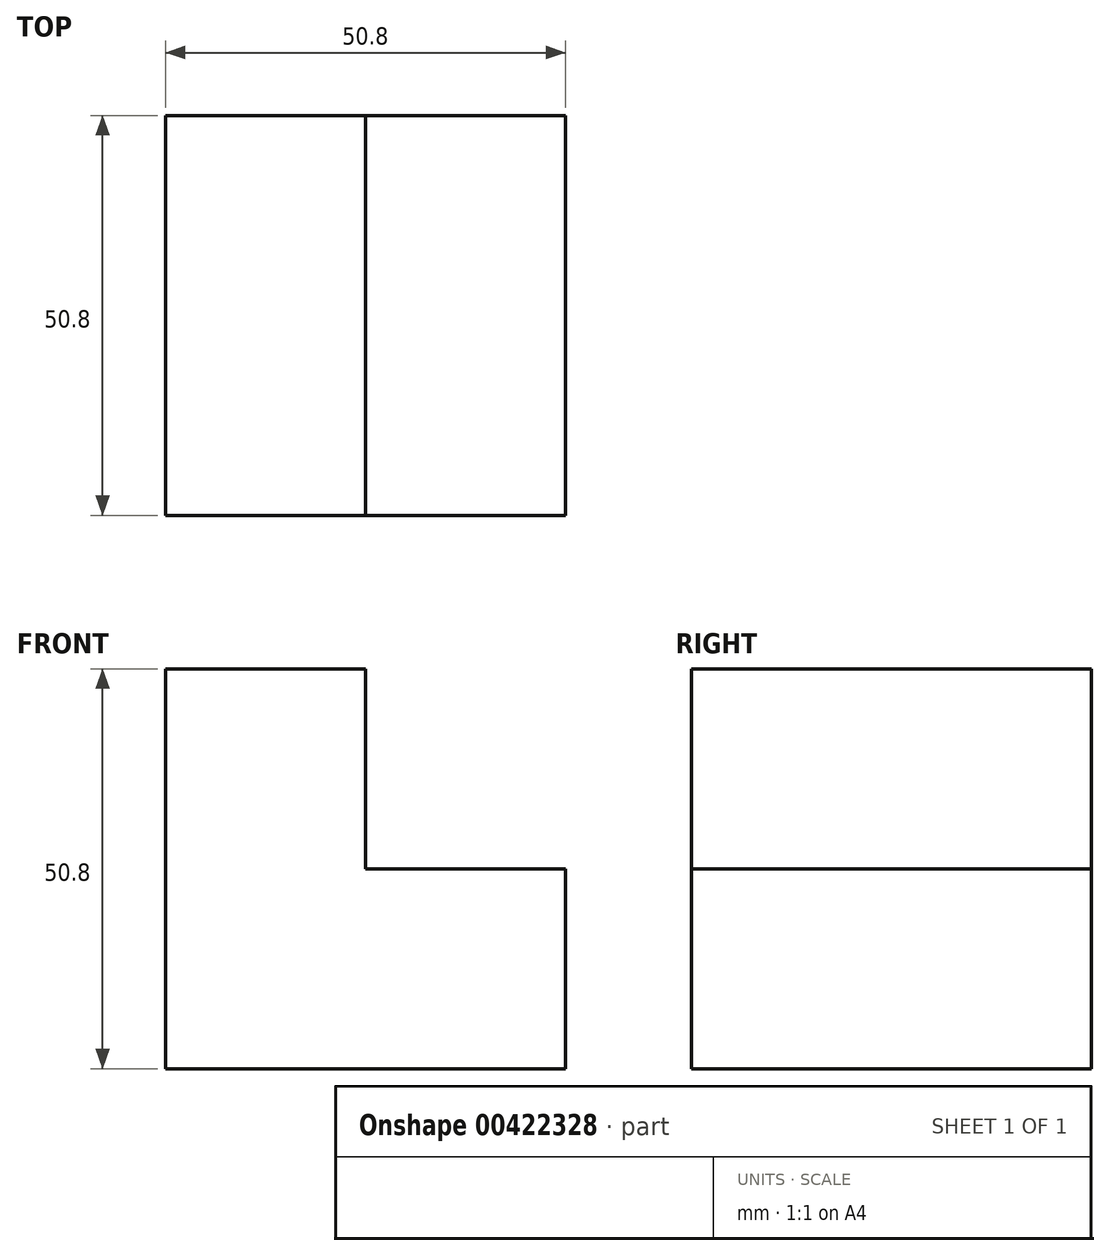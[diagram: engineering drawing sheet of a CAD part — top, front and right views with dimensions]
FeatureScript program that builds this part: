
annotation { "Feature Type Name" : "Feature", "Feature Type Description" : "" }
export const myFeature = defineFeature(function(context is Context, id is Id, definition is map)
    precondition{}
    {
        {
            var Q0;
            Q0=qCreatedBy(makeId("Front.planeOp"),FACE);
            var sketch = newSketch(context, id + "F0", { "sketchPlane" : qUnion([Q0])});
            skPoint(sketch, "E0.start.orphan", {"position": v(-50.8, 50.8) * mm});
            skPoint(sketch, "E1.end.orphan", {"position": v(-50.8, 0) * mm});
            skLineSegment(sketch, "E2", {"start": v(0, 0) * mm, "end": v(-50.8, 0) * mm});
            skLineSegment(sketch, "E3", {"start": v(-50.8, 50.8) * mm, "end": v(-50.8, 0) * mm});
            skLineSegment(sketch, "E4", {"start": v(-25.4, 50.8) * mm, "end": v(-50.8, 50.8) * mm});
            skLineSegment(sketch, "E5", {"start": v(-25.4, 50.8) * mm, "end": v(-25.4, 25.4) * mm});
            skLineSegment(sketch, "E6", {"start": v(-25.4, 25.4) * mm, "end": v(0, 25.4) * mm});
            skLineSegment(sketch, "E7", {"start": v(0, 25.4) * mm, "end": v(0, 0) * mm});
            skSolve(sketch);
        }
        {
            var Q0;
            Q0=makeQuery(id+"F0.imprint","IMPRINT",FACE,{"disambiguationData":[TD([[makeQuery(id+"F0.imprint","IMPRINT",EDGE,{"derivedFrom":sQuery(id+"F0.wireOp",EDGE,"E2")}),-1.0]])]});
            extrude(context, id + "F1", {"entities" : qUnion([Q0]), "depth" : 50.8 * mm});
        }
        {
            var Q0;
            Q0 = qSketchRegion(id + "F0", true);
            extrude(context, id + "F2", {"entities" : qUnion([Q0]), "operationType" : NewBodyOperationType.ADD, "depth" : 25.4 * mm});
        }
    });
